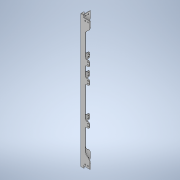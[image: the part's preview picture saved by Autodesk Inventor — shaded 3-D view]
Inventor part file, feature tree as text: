
AUTODESK INVENTOR PART (.ipt)
format: ipt  version: 2022 (Build 260153000, 153)  size: 458,240 bytes
history: native  units: mm
features: extrude x10, sketch x9, projected_geometry x3, chamfer x2, other x1
ambient origin geometry x8: Origin, YZ Plane, XZ Plane, XY Plane, X Axis, Y Axis, Z Axis, Center Point
bodies: Solid1 (feature_tree)
feature tree (25):
  extrude  "Extrusion1"  Depth=1.0mm TaperAngle=45.0deg
  chamfer  "Chamfer1"  Distance=1.2mm
  extrude  "Extrusion2"  Depth=1.2mm TaperAngle=0.0deg
  extrude  "Extrusion3"  Depth=6.5mm TaperAngle=0.0deg
  extrude  "Extrusion4"  Depth=2.0mm
  extrude  "Extrusion5"  Depth=5.0mm
  extrude  "Extrusion6"  Depth=6.5mm
  chamfer  "Chamfer2"  Distance=7.0mm
  extrude  "Extrusion7"  Depth=1.2mm
  extrude  "Extrusion8"  Depth=1.2mm
  extrude  "Extrusion9"  Depth=1.2mm
  extrude  "Extrusion10"  Depth=1.2mm
  sketch  "Sketch1"  dims[d0=12.5mm d1=0.0mm d2=1.0mm d3=2.0mm d4=45.0deg d5=1.2mm d6=0.0mm]
  projected_geometry  "Projected Loop1"
  sketch  "Sketch2"  dims[d7=1.2mm d8=0.0mm d9=1.2mm d10=0.0mm]
  sketch  "Sketch3"  dims[d11=1.2mm d12=0.0mm d13=6.5mm d14=7.0mm d15=0.0mm d16=0.0mm]
  sketch  "Sketch4"  dims[d17=1.0mm d18=2.0mm d19=45.0deg d20=3.0mm]
  sketch  "Sketch5"  dims[d21=19.5mm d22=5.0mm]
  sketch  "Sketch6"  dims[d23=6.5mm d24=0.0mm d25=3.0mm]
  projected_geometry  "Projected Loop2"
  sketch  "Sketch8"  dims[d26=7.0mm]
  sketch  "Sketch9"  dims[d27=3.0mm]
  projected_geometry  "Projected Loop3"
  sketch  "Sketch10"  dims[d28=3.0mm d29=7.0mm d30=19.5mm d31=5.0mm d32=5.0mm d33=3.0mm d34=3.0mm d35=19.5mm d36=7.0mm d37=5.0mm d38=5.0mm d39=3.0mm d40=3.0mm d41=19.5mm d42=7.0mm d43=5.0mm d44=5.0mm d45=6.5mm d46=0.0mm d47=3.0mm d48=96.0mm d49=19.5mm d50=8.0mm d51=4.0mm d52=1.2mm d53=0.0mm d54=3.0mm d55=6.4mm d56=8.0mm d57=4.0mm d58=3.0mm d59=194.6mm d60=8.0mm d61=3.0mm d62=6.4mm d63=8.0mm d64=4.0mm d65=3.0mm d66=243.9mm d67=3.0mm d68=6.4mm d69=8.0mm d70=8.0mm d71=4.0mm d72=3.0mm d73=96.0mm d74=19.5mm d75=8.0mm d76=4.0mm d77=3.0mm d78=6.4mm d79=8.0mm d80=4.0mm d81=3.0mm d82=194.6mm d83=8.0mm d84=3.0mm d85=6.4mm d86=8.0mm d87=4.0mm d88=3.0mm d89=243.9mm d90=3.0mm d91=6.4mm d92=8.0mm d93=8.0mm d94=4.0mm d95=1.0mm d96=1.2mm d97=0.0mm]
  other  "Ñêðóãëåíèå2"
